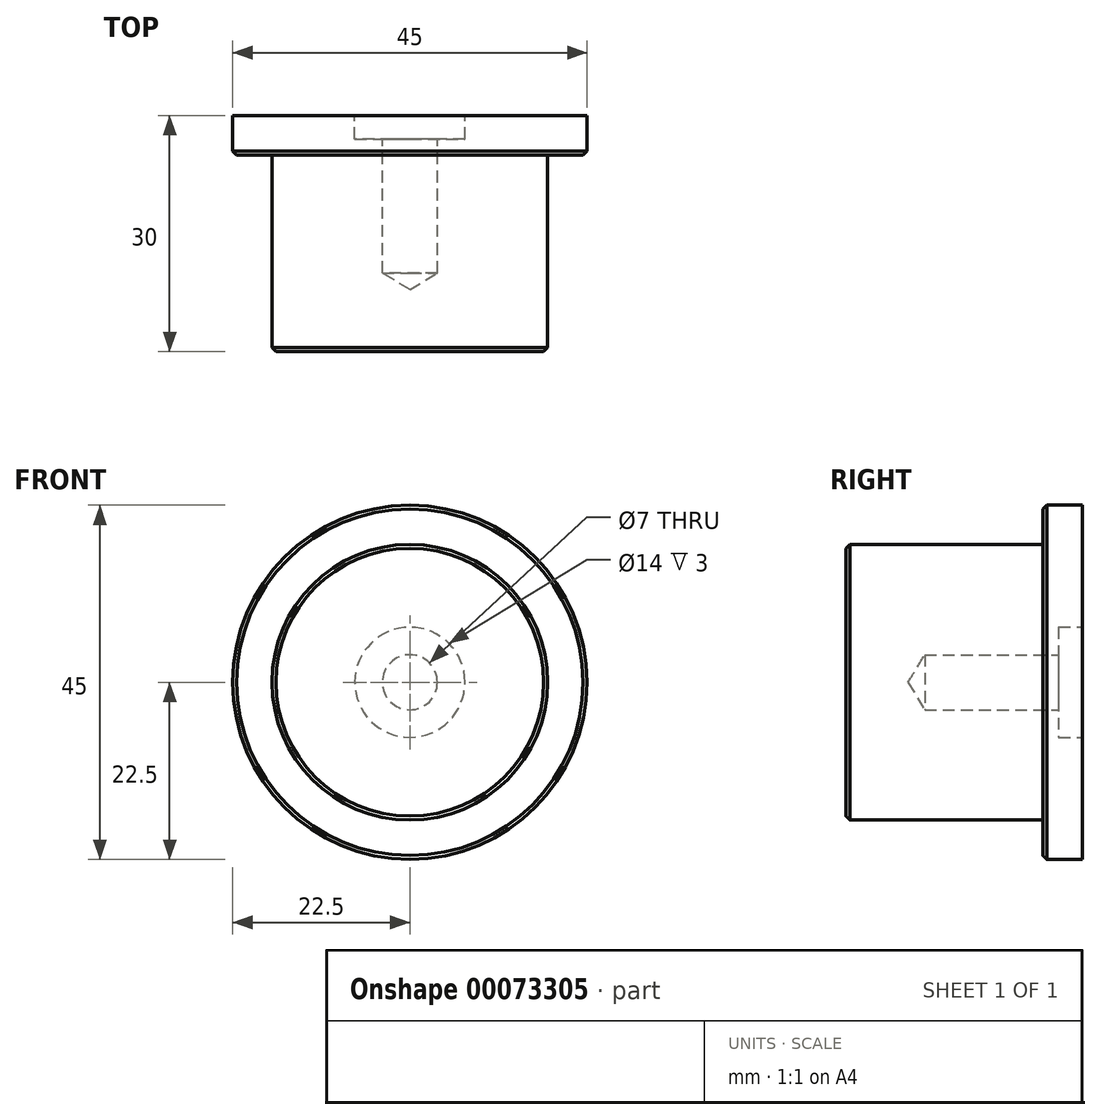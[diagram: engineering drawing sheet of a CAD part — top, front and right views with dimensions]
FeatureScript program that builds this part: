
annotation { "Feature Type Name" : "Feature", "Feature Type Description" : "" }
export const myFeature = defineFeature(function(context is Context, id is Id, definition is map)
    precondition{}
    {
        {
            var Q0;
            Q0=qCreatedBy(makeId("Front.planeOp"),FACE);
            var sketch = newSketch(context, id + "F0", { "sketchPlane" : qUnion([Q0])});
            skCircle(sketch, "E0", {"center": v(0, 0) * mm, "radius": 22.5 * mm});
            skCircle(sketch, "E1", {"center": v(0, 0) * mm, "radius": 17.5 * mm});
            skSolve(sketch);
        }
        {
            var Q0;
            Q0=makeQuery(id+"F0.imprint","IMPRINT",FACE,{"disambiguationData":[TD([[makeQuery(id+"F0.imprint","IMPRINT",EDGE,{"derivedFrom":sQuery(id+"F0.wireOp",EDGE,"E1")}),1.0]])]});
            extrude(context, id + "F1", {"entities" : qUnion([Q0]), "depth" : 30 * mm});
        }
        {
            var Q0;
            Q0 = qSketchRegion(id + "F0", true);
            extrude(context, id + "F2", {"entities" : qUnion([Q0]), "operationType" : NewBodyOperationType.ADD, "depth" : 5 * mm});
        }
        {
            var Q0;
            {var subQ0=sQuery(id+"F0.wireOp",EDGE,"E1");Q0=makeQuery(id+"F2.boolean.opBoolean","MERGE",FACE,{"derivedFrom":[makeQuery(id+"F1.opExtrude","CAP_FACE",FACE,{"disambiguationData":[OSD([subQ0])],"isStart":true}),makeQuery(id+"F2.opExtrude","CAP_FACE",FACE,{"disambiguationData":[OSD([sQuery(id+"F0.wireOp",EDGE,"E0"),subQ0])],"isStart":true})]});}
            var sketch = newSketch(context, id + "F3", { "sketchPlane" : qUnion([Q0])});
            skPoint(sketch, "E2", {"position": v(0, 0) * mm});
            skSolve(sketch);
        }
        {
            var Q0;
            Q0=sQuery(id+"F3.wireOp",VERTEX,"E2");
            var Q1;
            Q1=makeQuery(id+"F1.opExtrude","SWEPT_BODY",BODY,{"disambiguationData":[OSD([sQuery(id+"F0.wireOp",EDGE,"E1")])]});
            hole(context, id + "F4", {"style" : HoleStyle.C_BORE, "endStyle" : HoleEndStyle.BLIND, "holeDiameter" : 7 * mm, "cBoreDiameter" : 14 * mm, "cBoreDepth" : 3 * mm, "holeDepth" : 20 * mm, "locations" : qUnion([Q0]), "scope" : qUnion([Q1])});
        }
        {
            var Q0;
            Q0=makeQuery(id+"F1.opExtrude","CAP_EDGE",EDGE,{"disambiguationData":[OSD([sQuery(id+"F0.wireOp",EDGE,"E1")])],"isStart":false});
            var Q1;
            Q1=makeQuery(id+"F2.opExtrude","CAP_EDGE",EDGE,{"disambiguationData":[OSD([sQuery(id+"F0.wireOp",EDGE,"E0")])],"isStart":false});
            chamfer(context, id + "F5", {"entities" : qUnion([Q0, Q1]), "width" : 0.5 * mm, "tangentPropagation" : true});
        }
    });
